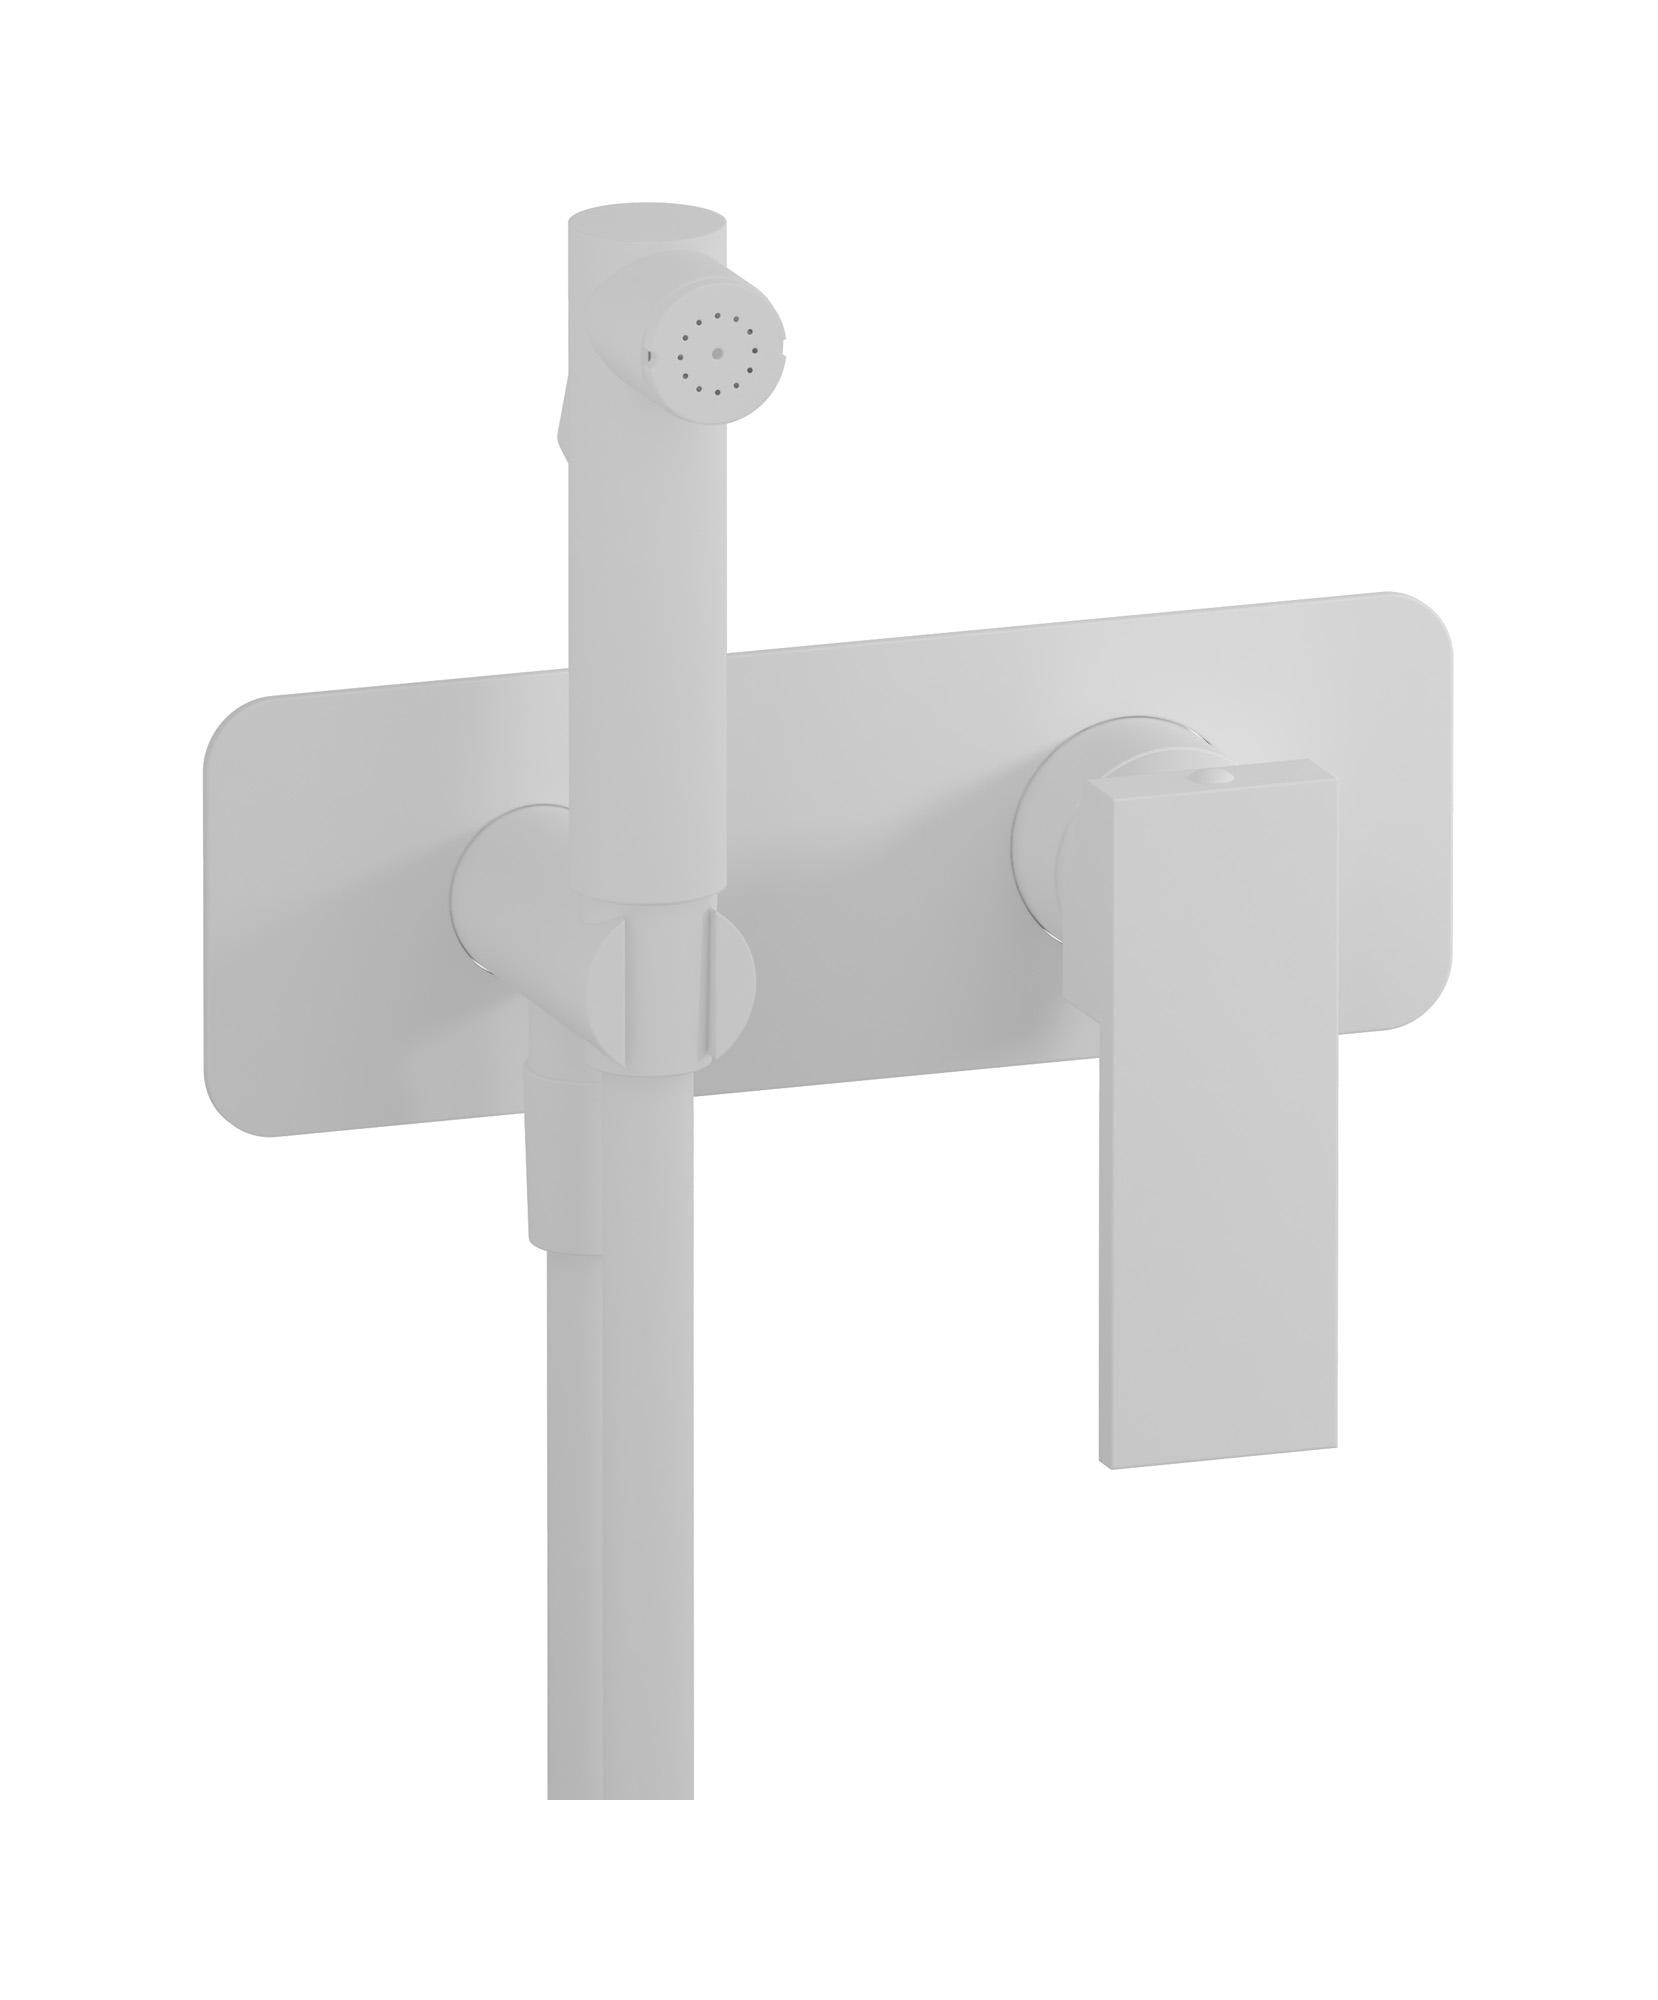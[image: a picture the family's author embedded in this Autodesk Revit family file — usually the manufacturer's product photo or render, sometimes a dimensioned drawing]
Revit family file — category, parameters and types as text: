
# Revit family: RU706
name_source: partatom
category: Apparecchi idraulici
units: mm (PartAtom-declared; Revit-internal decimal feet)

## family parameters
Basato su piano di lavoro = No
Condiviso = No
Mantieni orientamento annotazione = No
Numero OmniClass = 23.45.55.17
Punto di calcolo locali = No
Quota connettore circolare = Usa diametro
Sempre verticale = Sì
Taglio con vuoti quando caricato = No
Tipo di parte = Normale
Titolo OmniClass = Mixing Faucets

## types (12) — shared parameters
Cold water inlet = 10 mm  [stored 0.0328084 ft]
Commenti sul tipo = Exposed parts for bidet spray complete with mixer
Connessione CW = No
Connessione HW = No
Connessione di scarico = No
Connessione di ventilazione = No
Descrizione = Exposed parts for bidet spray complete with mixer
Hot water inlet = 10 mm  [stored 0.0328084 ft]
Produttore = IB Rubinetterie S.p.A.
URL = https://www.weareib.it
zero-valued in all types: Prospetto di default

## per-type parameters (varying)
| type | Finishes surface | Immagine tipo | Modello |
| Matt White | IB_matt white | RU706BO.jpg | RU706BO |
| Chrome | IB_Chrome | RU706CC.jpg | RU706CC |
| Black Chrome | IB_Black chrome | RU706CF.jpg | RU706CF |
| Brushed Black Chrome | IB_Brushed black chrome | RU706CS.jpg | RU706CS |
| Pale Gold | IB_Pale gold | RU706II.jpg | RU706II |
| Brushed Pale Gold | IB_brushed pale gold | RU706IS.jpg | RU706IS |
| Matt Black | IB_matt black | RU706NP.jpg | RU706NP |
| Gold | IB_gold | RU706OO.jpg | RU706OO |
| Brushed Gold | IB_brushed gold | RU706OS.jpg | RU706OS |
| Rose Gold | IB_Rose gold | RU706RS.jpg | RU706RS |
| Brushed Rose Gold | IB_Brushed rose gold | RU706SR.jpg | RU706SR |
| Brushed Nickel | IB_Brushed nickel | RU706SS.jpg | RU706SS |

note: [stored X ft] marks values corroborated as IEEE doubles in the binary element streams (Revit-internal decimal feet)
